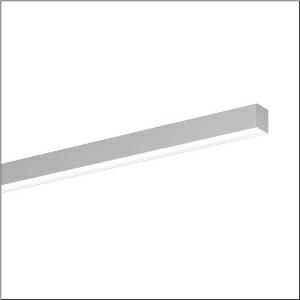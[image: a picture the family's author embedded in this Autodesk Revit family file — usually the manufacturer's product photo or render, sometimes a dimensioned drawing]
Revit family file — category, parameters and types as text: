
# Revit family: silica_r__21_51mx23dn47sb_d936
name_source: partatom
category: Lighting Fixtures
units: mm (PartAtom-declared; Revit-internal decimal feet)

## family parameters
Cut with Voids When Loaded = No
Host = Face
Light Source = No
Part Type = Normal
Room Calculation Point = No
Round Connector Dimension = Use Diameter
Shared = No

## types (1)
- --- (1 x LED, 7380 lm, 51.1 W, 4000K)
    Apparent Load = 51 VA
    CIE Flux Codes = 78 96 99 100 100
    Color Rendering = 80
    Color Temperature = 4000K
    Default Elevation = 1800 mm
    Description = Silica® 21, office luminaire, primary optical cover: prismatic diffuser, of PMMA, CAT 2 (L<= 3000cd/m²), light emission: direct distribution, primary light characteristic: symmetric, installation type: surface-mounted, LED, rated luminous flux: 7.380lm, luminous efficacy: 144lm/W, light colour: 840, colour temperature: 4000K, control gear: DALI 2, with terminal, 3+2-pole, max. 2.5mm², mains connection: 220..240V, AC, 50/60Hz, rated input power: 51.1W, luminaire housing, of aluminium, traffic white (RAL 9016), length: 2.700mm, width: 53mm, height: 53mm, protection rating (complete): IP20, insulation class (complete): insulation class I (protective earthing), certification: CE, permissible operating ambient temperature: 0..+35°C, standard: EN 50419, packaging unit: 1 piece
    Height = 53 mm
    Lamp = 1 x LED
    Lamp Light Flux = 7380 lm
    Lamp Power = 51.1 W
    Lamp count = 1
    Length = 2704 mm
    Luminous efficacy = 144 lm/W
    Manufacturer = Siteco
    ModVariant = No
    Model = 51MX23DN47SB
    Mounting Place = Ceiling
    Mounting Type = Surface mounted
    Number of Poles = 1
    OnlyDefault = Yes
    Power Factor = 1
    Product Name = Silica® 21
    Product group = office luminaire | ceiling mounted
    ProductGroupID = 303
    Protection Class = Protection class I
    Protection Degree = IP 20
    RLX_Detail_Level = 1
    RLX_Emergency_Light_Flux = 0 lm
    RLX_Emergency_Type = 0
    RLX_Emergency_Type_DB = No
    RlxData = <blob elided: 20157 chars, md5=69825620>
    Socket = socket
    Standby Power = 0 W
    System Light Flux = 7380 lm
    System Power = 51 W
    Type Comments = factory setting: luminous flux: 100 % | dim-lin: 254 | 323 mA
    Type Image = l_1335933.jpg
    URL = http://relux.com
    VarID = @adj_084155
    Voltage = 0 V
    Weight = 0.00 kg
    Width = 53 mm

## geometry (parser evidence)
native form markers: Blend x4, Sweep x12
no freeform markers — native parametric forms only
